# Revit family: Haworth_XSeries_ComboValet_36Wide
name_source: partatom
category: Furniture Systems
revit_build: Autodesk Revit 2018 (Build: 20170223_1515(x64)
units: mm (PartAtom-declared; Revit-internal decimal feet)

## family parameters
Always vertical = Yes
Cut with Voids When Loaded = No
OmniClass Number = 23.40.70.14.64.21
OmniClass Title = Systems Furniture
Part Type = Normal
Room Calculation Point = No
Round Connector Dimension = Use Diameter
Shared = No
Work Plane-Based = No

## types (2) — shared parameters
Actual Depth = 18 3/4"
Actual Height = 63 1/2"
Actual Width = 29 7/8"
Assembly Code = E2020200
Cabinet Height = 39 1/2"
Classic Pull = No
Crescent Pull = No
Description = Haworth X Series Combo Unit Valet - 18d 30w 63h
Door Height = 60 1/8"
Door Height 2 = 23 3/4"
Door Width = 14 7/8"
Drawer 1 Height = 12"
Drawer 2 Height = 11 7/8"
Drawer 3 Height = 12"
Drawer 4 Height = 5 15/16"
Drawer Width = 14 7/8"
Ellipse Pull = No
J Pull = No
Linear Pull = Yes
Manufacturer = Haworth
Max. Height = 63 1/2"
Max. Width = 47 7/8"
Min. Height = 27 1/2"
Min. Width = 29 7/8"
Model = JVP
Pull Finish = Haworth _ Metal _ Brushed Aluminum
Pull Height Centerline = 48 1/4"
Pull Height Centerline 2 = 11 7/8"
Radius Pull = No
Revision Number = 4
Shelf Depth = 13 1/2"
Shelf Width = 17 1/4"
Size = Verify Final Dim. w/ Haworth
Sustainability Info = https://www.haworth.com
Taper Pull = No
Top Height = 24"
Touch Latch = No
URL = http://www.haworth.com
URL - Product = https://www.haworth.com
Warranty = http://www.haworth.com

## per-type parameters (varying)
| type | Box Box File File | File File File |
| 18d 30w 63h - Valet Storage Box Box File File | Yes | No |
| 18d 30w 63h - Valet Storage File File File | No | Yes |

## geometry (parser evidence)
native form markers: Sweep x15
no freeform markers — native parametric forms only
